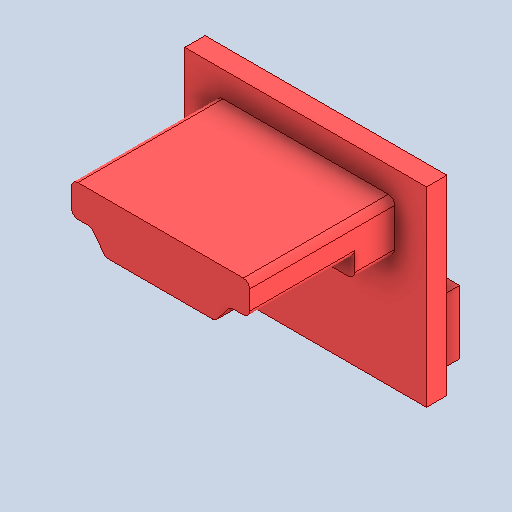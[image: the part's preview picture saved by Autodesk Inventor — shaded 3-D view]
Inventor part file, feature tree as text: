
AUTODESK INVENTOR PART (.ipt)
format: ipt  version: 2024.2 (Build 282272000, 272)  size: 167,424 bytes
history: native  units: mm
features: extrude x4, plane x1, fillet x1, sketch x1, projected_geometry x1
ambient origin geometry x8: Origin, YZ Plane, XZ Plane, XY Plane, X Axis, Y Axis, Z Axis, Center Point
bodies: Solid1 (feature_tree)
feature tree (8):
  extrude  "Extrusion1"  Depth=15.0mm
  extrude  "Extrusion2"  Depth=1.6mm TaperAngle=0.0deg
  plane  "Work Plane1"
  extrude  "Extrusion3"  Depth=5.0mm
  extrude  "Extrusion4"  Depth=1.0mm
  fillet  "Fillet1"  Radius=17.0mm
  sketch  "Sketch4"  dims[d0=19.0mm d1=15.0mm d2=1.6mm d3=0.0mm d4=5.0mm d5=1.0mm d6=17.0mm d7=2.0mm d8=0.0mm d9=14.0mm d10=4.0mm d11=2.0mm d12=-15.0mm d13=2.0mm d14=0.0mm d15=8.25mm d16=0.0mm d17=0.5mm]
  projected_geometry  "Projected Loop1"
